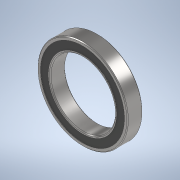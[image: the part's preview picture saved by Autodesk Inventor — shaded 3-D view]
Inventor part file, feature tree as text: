
AUTODESK INVENTOR PART (.ipt)
format: ipt  version: 2020.2 (Build 242310000, 310)  size: 606,720 bytes
history: native  units: in
note: dims shown in document units (in); Inventor stores cm internally (conversion verified against a paired STEP export)
features: other x11, revolve x5
ambient origin geometry x8: Origin, YZ Plane, XZ Plane, XY Plane, X Axis, Y Axis, Z Axis, Center Point
bodies: Solid1 (feature_tree), Solid2 (feature_tree), Solid3 (feature_tree), Solid4 (feature_tree), Solid5 (feature_tree), Solid6 (feature_tree), Solid7 (feature_tree), Solid8 (feature_tree), Solid9 (feature_tree), Solid10 (feature_tree), Solid11 (feature_tree), Solid12 (feature_tree), Solid13 (feature_tree), Solid14 (feature_tree), Solid15 (feature_tree), Solid16 (feature_tree)
feature tree (16):
  revolve  "Revolve1"  [1 undecoded]
  revolve  "Revolve3"  [1 undecoded]
  revolve  "Revolve4"  [1 undecoded]
  other  "CirPattern1[1]"
  other  "CirPattern1[2]"
  other  "CirPattern1[3]"
  other  "CirPattern1[4]"
  other  "CirPattern1[5]"
  other  "CirPattern1[6]"
  other  "CirPattern1[7]"
  other  "CirPattern1[8]"
  other  "CirPattern1[9]"
  other  "CirPattern1[10]"
  other  "CirPattern1[11]"
  revolve  "Revolve5[1]"  [1 undecoded]
  revolve  "Revolve5[2]"  [1 undecoded]
note: 5 required parameter values undecoded (feature->parameter linkage not recoverable at this tier; creation-order binding heuristic only, values carry confidence <= 0.55)
